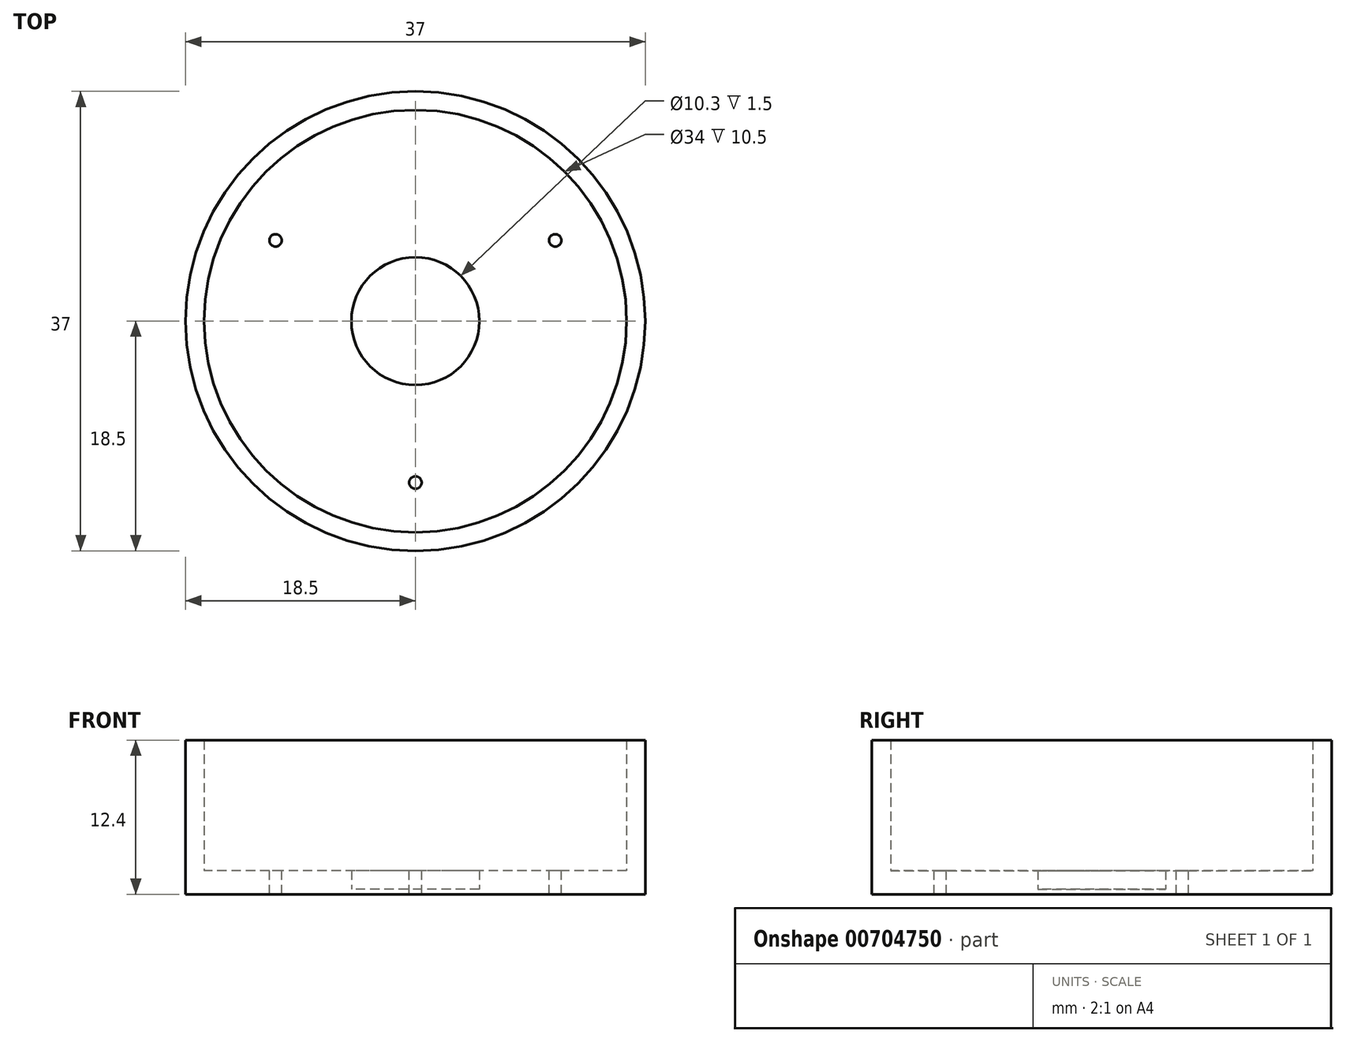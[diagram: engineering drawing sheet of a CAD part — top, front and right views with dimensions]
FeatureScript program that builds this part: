
annotation { "Feature Type Name" : "Feature", "Feature Type Description" : "" }
export const myFeature = defineFeature(function(context is Context, id is Id, definition is map)
    precondition{}
    {
        {
            assignVariable(context, id + "F0", {"name" : "btWandStaerke", "anyValue" : 1.5 * mm});
        }
        {
            assignVariable(context, id + "F1", {"name" : "folienStaerke", "anyValue" : 0.4 * mm});
        }
        {
            var Q0;
            Q0=qCreatedBy(makeId("Top.planeOp"),FACE);
            var sketch = newSketch(context, id + "F2", { "sketchPlane" : qUnion([Q0])});
            skCircle(sketch, "E0", {"center": v(0, 0) * mm, "radius": 5.15 * mm});
            skCircle(sketch, "E1", {"center": v(0, 0) * mm, "radius": 17 * mm});
            skCircle(sketch, "E2", {"center": v(0, 11) * mm, "radius": 5.15 * mm});
            skCircle(sketch, "E3", {"center": v(0, 0) * mm, "radius": 18.5 * mm});
            skCircle(sketch, "E4", {"center": v(0, -11) * mm, "radius": 5.15 * mm});
            skCircle(sketch, "E5", {"center": v(0, 0) * mm, "radius": 13 * mm, "construction": true});
            skLineSegment(sketch, "E6", {"start": v(0, 0) * mm, "end": v(25.72, 14.85) * mm, "construction": true});
            skLineSegment(sketch, "E7", {"start": v(0, 0) * mm, "end": v(-24.16, 13.95) * mm, "construction": true});
            skLineSegment(sketch, "E8", {"start": v(0, 0) * mm, "end": v(0, 23.96) * mm, "construction": true});
            skLineSegment(sketch, "E9", {"start": v(0, 0) * mm, "end": v(0, -25.55) * mm, "construction": true});
            skCircle(sketch, "E10", {"center": v(-11.26, 6.5) * mm, "radius": 0.5 * mm});
            skCircle(sketch, "E11", {"center": v(11.26, 6.5) * mm, "radius": 0.5 * mm});
            skCircle(sketch, "E12", {"center": v(0, -13) * mm, "radius": 0.5 * mm});
            skSolve(sketch);
        }
        {
            var Q0;
            Q0=makeQuery(id+"F2.imprint","IMPRINT",FACE,{"disambiguationData":[TD([[makeQuery(id+"F2.imprint","IMPRINT",EDGE,{"derivedFrom":sQuery(id+"F2.wireOp",EDGE,"E0")}),-1.0]])]});
            var Q1;
            Q1=makeQuery(id+"F2.imprint","IMPRINT",FACE,{"disambiguationData":[TD([[makeQuery(id+"F2.imprint","IMPRINT",EDGE,{"derivedFrom":sQuery(id+"F2.wireOp",EDGE,"E0")}),1.0]])]});
            var Q2;
            Q2=makeQuery(id+"F2.imprint","IMPRINT",FACE,{"disambiguationData":[TD([[makeQuery(id+"F2.imprint","IMPRINT",EDGE,{"derivedFrom":sQuery(id+"F2.wireOp",EDGE,"E1")}),-1.0]])]});
            var Q3;
            Q3=makeQuery(id+"F2.imprint","IMPRINT",FACE,{"disambiguationData":[TD([[makeQuery(id+"F2.imprint","IMPRINT",EDGE,{"derivedFrom":sQuery(id+"F2.wireOp",EDGE,"E2")}),1.0]])]});
            var Q4;
            Q4=makeQuery(id+"F2.imprint","IMPRINT",FACE,{"disambiguationData":[TD([[makeQuery(id+"F2.imprint","IMPRINT",EDGE,{"derivedFrom":sQuery(id+"F2.wireOp",EDGE,"E4")}),1.0]])]});
            extrude(context, id + "F3", {"entities" : qUnion([Q0, Q1, Q2, Q3, Q4]), "oppositeDirection" : true, "depth" : getVariable(context, 'folienStaerke'), "offsetDistance" : 25 * mm});
        }
        {
            var Q0;
            Q0=makeQuery(id+"F2.imprint","IMPRINT",FACE,{"disambiguationData":[TD([[makeQuery(id+"F2.imprint","IMPRINT",EDGE,{"derivedFrom":sQuery(id+"F2.wireOp",EDGE,"E0")}),-1.0]])]});
            var Q1;
            Q1=makeQuery(id+"F2.imprint","IMPRINT",FACE,{"disambiguationData":[TD([[makeQuery(id+"F2.imprint","IMPRINT",EDGE,{"derivedFrom":sQuery(id+"F2.wireOp",EDGE,"E2")}),1.0]])]});
            var Q2;
            Q2=makeQuery(id+"F2.imprint","IMPRINT",FACE,{"disambiguationData":[TD([[makeQuery(id+"F2.imprint","IMPRINT",EDGE,{"derivedFrom":sQuery(id+"F2.wireOp",EDGE,"E4")}),1.0]])]});
            extrude(context, id + "F4", {"entities" : qUnion([Q0, Q1, Q2]), "operationType" : NewBodyOperationType.ADD, "depth" : getVariable(context, 'btWandStaerke'), "offsetDistance" : 25 * mm});
        }
        {
            var Q0;
            Q0=makeQuery(id+"F2.imprint","IMPRINT",FACE,{"disambiguationData":[TD([[makeQuery(id+"F2.imprint","IMPRINT",EDGE,{"derivedFrom":sQuery(id+"F2.wireOp",EDGE,"E1")}),-1.0]])]});
            extrude(context, id + "F5", {"entities" : qUnion([Q0]), "operationType" : NewBodyOperationType.ADD, "depth" : 12 * mm, "offsetDistance" : 25 * mm});
        }
    });
